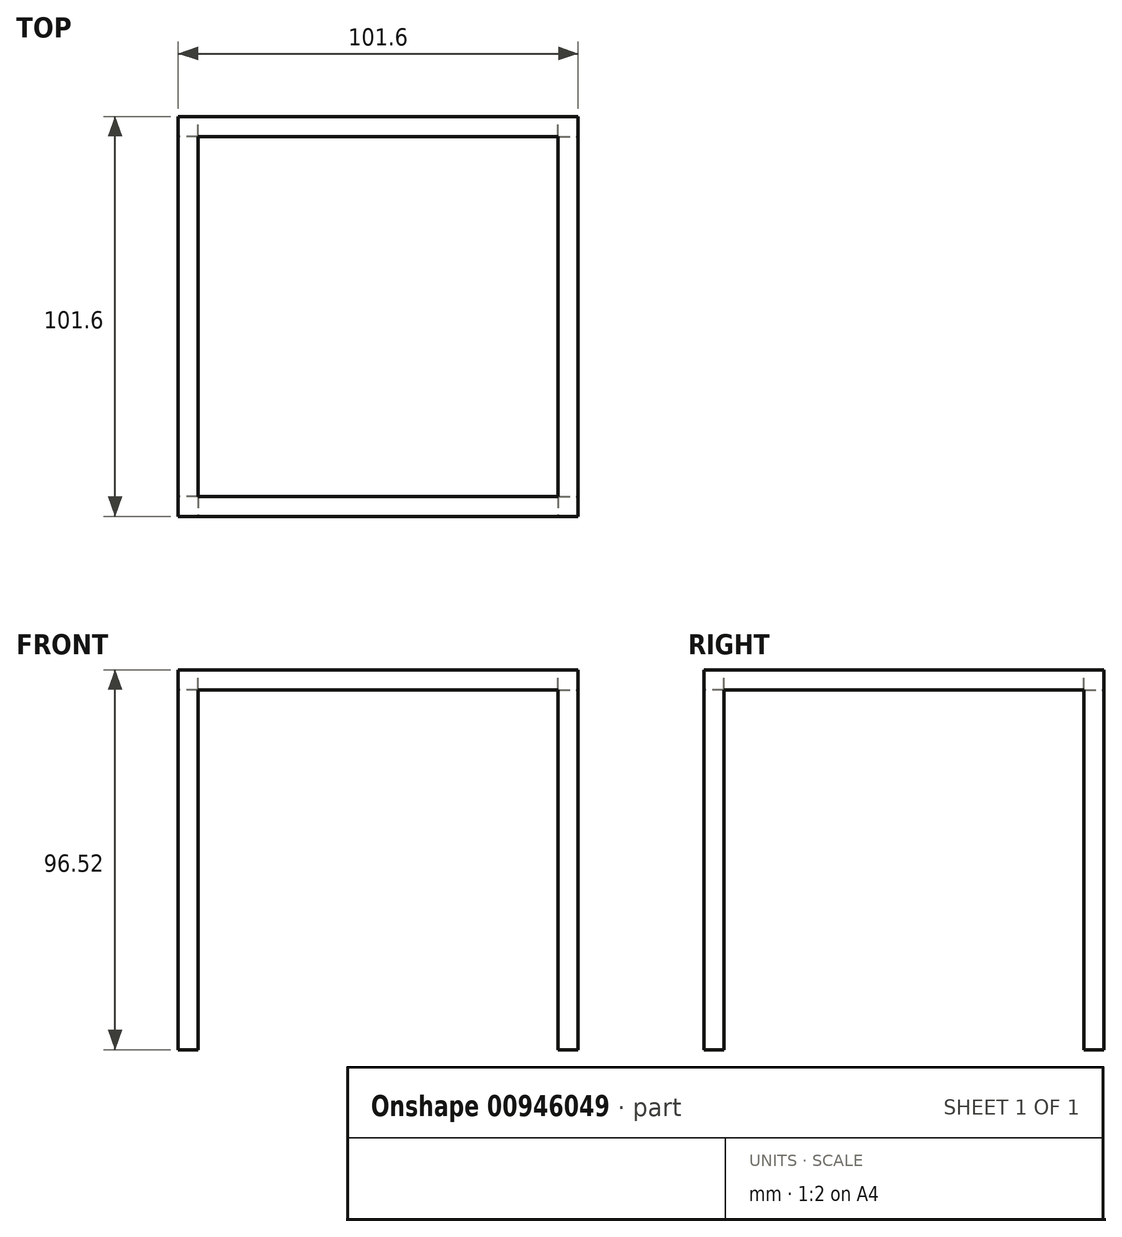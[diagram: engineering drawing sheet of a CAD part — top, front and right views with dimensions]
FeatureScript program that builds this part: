
annotation { "Feature Type Name" : "Feature", "Feature Type Description" : "" }
export const myFeature = defineFeature(function(context is Context, id is Id, definition is map)
    precondition{}
    {
        {
            var Q0;
            Q0=qCreatedBy(makeId("Top.planeOp"),FACE);
            var sketch = newSketch(context, id + "F0", { "sketchPlane" : qUnion([Q0])});
            skLineSegment(sketch, "E0.bottom", {"start": v(50.8, -50.8) * mm, "end": v(-50.8, -50.8) * mm});
            skLineSegment(sketch, "E0.top", {"start": v(50.8, 50.8) * mm, "end": v(-50.8, 50.8) * mm});
            skLineSegment(sketch, "E0.left", {"start": v(50.8, -50.8) * mm, "end": v(50.8, 50.8) * mm});
            skLineSegment(sketch, "E0.right", {"start": v(-50.8, -50.8) * mm, "end": v(-50.8, 50.8) * mm});
            skPoint(sketch, "E0.middle", {"position": v(0, 0) * mm});
            skLineSegment(sketch, "E1.bottom", {"start": v(45.72, -45.72) * mm, "end": v(-45.72, -45.72) * mm});
            skLineSegment(sketch, "E1.top", {"start": v(45.72, 45.72) * mm, "end": v(-45.72, 45.72) * mm});
            skLineSegment(sketch, "E1.left", {"start": v(45.72, -45.72) * mm, "end": v(45.72, 45.72) * mm});
            skLineSegment(sketch, "E1.right", {"start": v(-45.72, -45.72) * mm, "end": v(-45.72, 45.72) * mm});
            skLineSegment(sketch, "E2", {"start": v(-45.72, 45.72) * mm, "end": v(-45.72, 50.8) * mm});
            skLineSegment(sketch, "E3", {"start": v(-45.72, 45.72) * mm, "end": v(-50.8, 45.72) * mm});
            skLineSegment(sketch, "E4", {"start": v(45.72, 45.72) * mm, "end": v(45.72, 50.8) * mm});
            skLineSegment(sketch, "E5", {"start": v(45.72, 45.72) * mm, "end": v(50.8, 45.72) * mm});
            skLineSegment(sketch, "E6", {"start": v(-45.72, -45.72) * mm, "end": v(-45.72, -50.8) * mm});
            skLineSegment(sketch, "E7", {"start": v(-45.72, -45.72) * mm, "end": v(-50.8, -45.72) * mm});
            skLineSegment(sketch, "E8", {"start": v(45.72, -45.72) * mm, "end": v(45.72, -50.8) * mm});
            skLineSegment(sketch, "E9", {"start": v(45.72, -45.72) * mm, "end": v(50.8, -45.72) * mm});
            skSolve(sketch);
        }
        {
            var Q0;
            {var subQ3=sQuery(id+"F0.wireOp",EDGE,"E4");Q0=makeQuery(id+"F0.imprint","IMPRINT",FACE,{"disambiguationData":[TD([[makeQuery(id+"F0.imprint","IMPRINT",EDGE,{"derivedFrom":subQ3}),-1.0]])]});}
            var Q1;
            Q1=makeQuery(id+"F0.imprint","IMPRINT",FACE,{"disambiguationData":[TD([[makeQuery(id+"F0.imprint","IMPRINT",EDGE,{"derivedFrom":sQuery(id+"F0.wireOp",EDGE,"E1.left")}),-1.0]])]});
            var Q2;
            Q2=makeQuery(id+"F0.imprint","IMPRINT",FACE,{"disambiguationData":[TD([[makeQuery(id+"F0.imprint","IMPRINT",EDGE,{"derivedFrom":sQuery(id+"F0.wireOp",EDGE,"E1.bottom")}),1.0]])]});
            var Q3;
            {var subQ3=sQuery(id+"F0.wireOp",EDGE,"E2");Q3=makeQuery(id+"F0.imprint","IMPRINT",FACE,{"disambiguationData":[TD([[makeQuery(id+"F0.imprint","IMPRINT",EDGE,{"derivedFrom":subQ3}),1.0]])]});}
            var Q4;
            Q4=makeQuery(id+"F0.imprint","IMPRINT",FACE,{"disambiguationData":[TD([[makeQuery(id+"F0.imprint","IMPRINT",EDGE,{"derivedFrom":sQuery(id+"F0.wireOp",EDGE,"E1.top")}),-1.0]])]});
            var Q5;
            {var subQ3=sQuery(id+"F0.wireOp",EDGE,"E8");Q5=makeQuery(id+"F0.imprint","IMPRINT",FACE,{"disambiguationData":[TD([[makeQuery(id+"F0.imprint","IMPRINT",EDGE,{"derivedFrom":subQ3}),1.0]])]});}
            var Q6;
            {var subQ3=sQuery(id+"F0.wireOp",EDGE,"E6");Q6=makeQuery(id+"F0.imprint","IMPRINT",FACE,{"disambiguationData":[TD([[makeQuery(id+"F0.imprint","IMPRINT",EDGE,{"derivedFrom":subQ3}),-1.0]])]});}
            var Q7;
            Q7=makeQuery(id+"F0.imprint","IMPRINT",FACE,{"disambiguationData":[TD([[makeQuery(id+"F0.imprint","IMPRINT",EDGE,{"derivedFrom":sQuery(id+"F0.wireOp",EDGE,"E1.right")}),1.0]])]});
            extrude(context, id + "F1", {"entities" : qUnion([Q0, Q1, Q2, Q3, Q4, Q5, Q6, Q7]), "oppositeDirection" : true, "depth" : 5.08 * mm, "offsetDistance" : 25.4 * mm});
        }
        {
            var Q0;
            {var subQ3=sQuery(id+"F0.wireOp",EDGE,"E6");Q0=makeQuery(id+"F0.imprint","IMPRINT",FACE,{"disambiguationData":[TD([[makeQuery(id+"F0.imprint","IMPRINT",EDGE,{"derivedFrom":subQ3}),-1.0]])]});}
            var Q1;
            {var subQ3=sQuery(id+"F0.wireOp",EDGE,"E4");Q1=makeQuery(id+"F0.imprint","IMPRINT",FACE,{"disambiguationData":[TD([[makeQuery(id+"F0.imprint","IMPRINT",EDGE,{"derivedFrom":subQ3}),-1.0]])]});}
            var Q2;
            {var subQ3=sQuery(id+"F0.wireOp",EDGE,"E8");Q2=makeQuery(id+"F0.imprint","IMPRINT",FACE,{"disambiguationData":[TD([[makeQuery(id+"F0.imprint","IMPRINT",EDGE,{"derivedFrom":subQ3}),1.0]])]});}
            var Q3;
            {var subQ3=sQuery(id+"F0.wireOp",EDGE,"E2");Q3=makeQuery(id+"F0.imprint","IMPRINT",FACE,{"disambiguationData":[TD([[makeQuery(id+"F0.imprint","IMPRINT",EDGE,{"derivedFrom":subQ3}),1.0]])]});}
            extrude(context, id + "F2", {"entities" : qUnion([Q0, Q1, Q2, Q3]), "operationType" : NewBodyOperationType.ADD, "oppositeDirection" : true, "depth" : 96.52 * mm, "offsetDistance" : 25.4 * mm});
        }
    });
